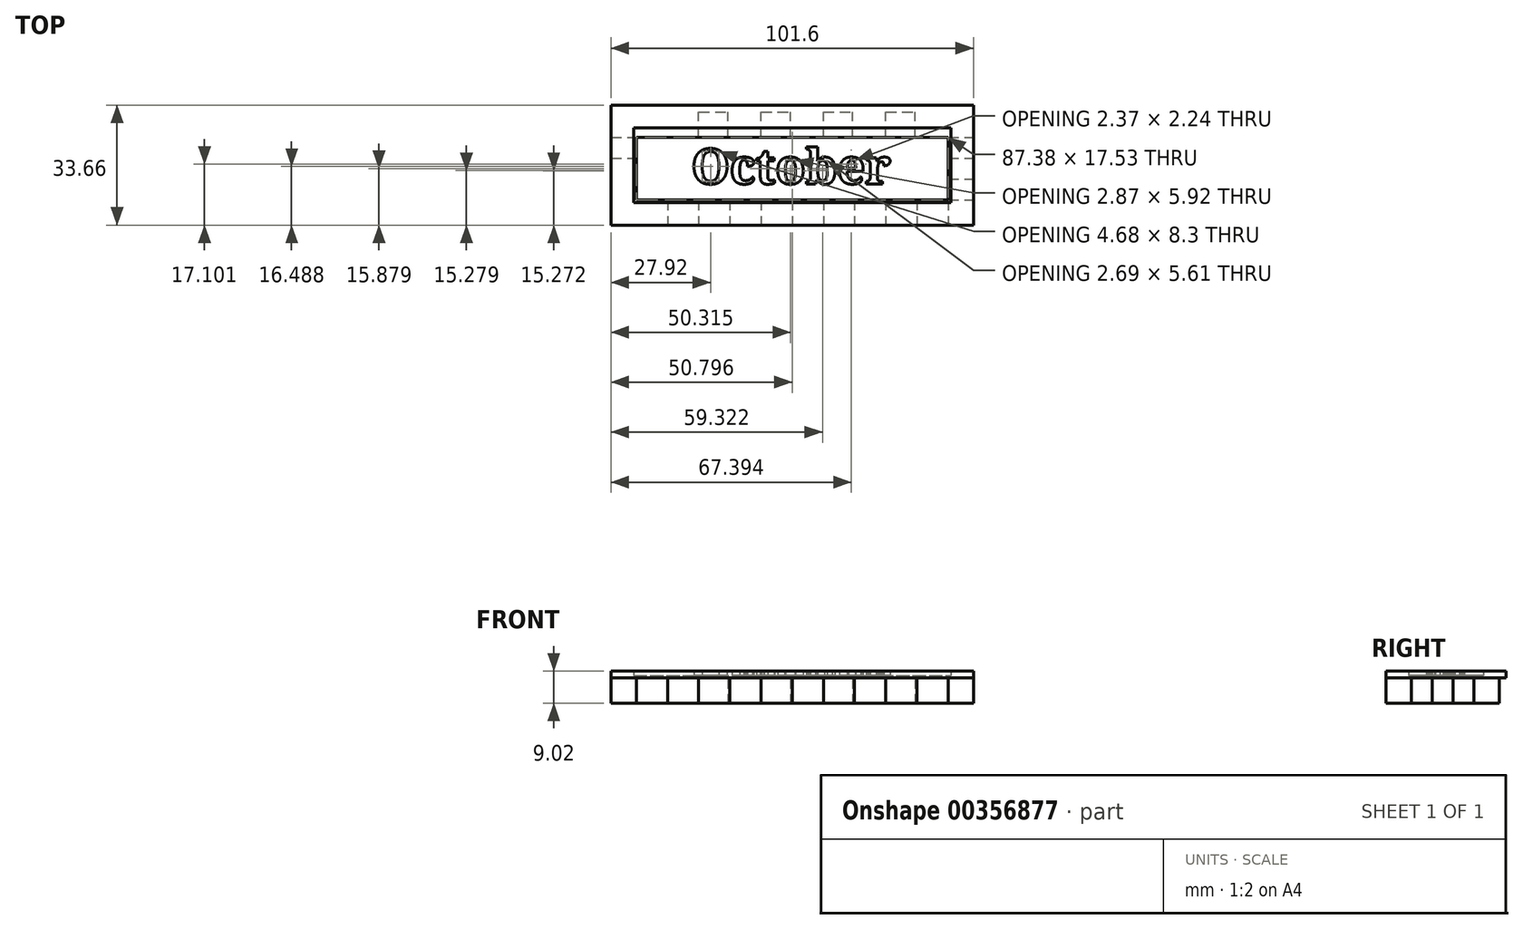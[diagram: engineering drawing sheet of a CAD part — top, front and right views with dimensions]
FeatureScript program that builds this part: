
annotation { "Feature Type Name" : "Feature", "Feature Type Description" : "" }
export const myFeature = defineFeature(function(context is Context, id is Id, definition is map)
    precondition{}
    {
        {
            var Q0;
            Q0=qCreatedBy(makeId("Top.planeOp"),FACE);
            var sketch = newSketch(context, id + "F0", { "sketchPlane" : qUnion([Q0])});
            skLineSegment(sketch, "E0.bottom", {"start": v(-52.12, 11.37) * mm, "end": v(49.48, 11.37) * mm});
            skLineSegment(sketch, "E0.top", {"start": v(-52.12, -20.38) * mm, "end": v(49.48, -20.38) * mm});
            skLineSegment(sketch, "E0.left", {"start": v(-52.12, 11.37) * mm, "end": v(-52.12, -20.38) * mm});
            skLineSegment(sketch, "E0.right", {"start": v(49.48, 11.37) * mm, "end": v(49.48, -20.38) * mm});
            skLineSegment(sketch, "E1.bottom", {"start": v(-52.12, 11.37) * mm, "end": v(-45.01, 11.37) * mm});
            skLineSegment(sketch, "E1.top", {"start": v(-52.12, 4.26) * mm, "end": v(-45.01, 4.26) * mm});
            skLineSegment(sketch, "E1.left", {"start": v(-52.12, 11.37) * mm, "end": v(-52.12, 4.26) * mm});
            skLineSegment(sketch, "E1.right", {"start": v(-45.01, 11.37) * mm, "end": v(-45.01, 4.26) * mm});
            skLineSegment(sketch, "E2.bottom", {"start": v(-45.01, 11.37) * mm, "end": v(-36.78, 11.37) * mm});
            skLineSegment(sketch, "E2.top", {"start": v(-45.01, 4.26) * mm, "end": v(-36.78, 4.26) * mm});
            skLineSegment(sketch, "E2.right", {"start": v(-36.78, 11.37) * mm, "end": v(-36.78, 4.26) * mm});
            skLineSegment(sketch, "E3.bottom", {"start": v(-36.78, 4.26) * mm, "end": v(-27.54, 4.26) * mm});
            skLineSegment(sketch, "E3.top", {"start": v(-36.78, 11.37) * mm, "end": v(-27.54, 11.37) * mm});
            skLineSegment(sketch, "E3.left", {"start": v(-36.78, 4.26) * mm, "end": v(-36.78, 11.37) * mm});
            skLineSegment(sketch, "E3.right", {"start": v(-27.54, 4.26) * mm, "end": v(-27.54, 11.37) * mm});
            skLineSegment(sketch, "E4.bottom", {"start": v(-27.54, 4.26) * mm, "end": v(-19.3, 4.26) * mm});
            skLineSegment(sketch, "E4.top", {"start": v(-27.54, 11.37) * mm, "end": v(-19.3, 11.37) * mm});
            skLineSegment(sketch, "E4.right", {"start": v(-19.3, 4.26) * mm, "end": v(-19.3, 11.37) * mm});
            skLineSegment(sketch, "E5.bottom", {"start": v(-19.3, 4.26) * mm, "end": v(-10.06, 4.26) * mm});
            skLineSegment(sketch, "E5.top", {"start": v(-19.3, 11.37) * mm, "end": v(-10.06, 11.37) * mm});
            skLineSegment(sketch, "E5.right", {"start": v(-10.06, 4.26) * mm, "end": v(-10.06, 11.37) * mm});
            skLineSegment(sketch, "E6.bottom", {"start": v(-10.06, 4.26) * mm, "end": v(-10.06, 4.26) * mm});
            skLineSegment(sketch, "E6.top", {"start": v(-10.06, 11.37) * mm, "end": v(-10.06, 11.37) * mm});
            skLineSegment(sketch, "E7.bottom", {"start": v(-10.06, 4.26) * mm, "end": v(-1.83, 4.26) * mm});
            skLineSegment(sketch, "E7.top", {"start": v(-10.06, 11.37) * mm, "end": v(-1.83, 11.37) * mm});
            skLineSegment(sketch, "E7.right", {"start": v(-1.83, 4.26) * mm, "end": v(-1.83, 11.37) * mm});
            skLineSegment(sketch, "E8.bottom", {"start": v(-1.83, 4.26) * mm, "end": v(7.41, 4.26) * mm});
            skLineSegment(sketch, "E8.top", {"start": v(-1.83, 11.37) * mm, "end": v(7.41, 11.37) * mm});
            skLineSegment(sketch, "E8.right", {"start": v(7.41, 4.26) * mm, "end": v(7.41, 11.37) * mm});
            skLineSegment(sketch, "E9.bottom", {"start": v(7.41, 4.26) * mm, "end": v(15.64, 4.26) * mm});
            skLineSegment(sketch, "E9.top", {"start": v(7.41, 11.37) * mm, "end": v(15.64, 11.37) * mm});
            skLineSegment(sketch, "E9.right", {"start": v(15.64, 4.26) * mm, "end": v(15.64, 11.37) * mm});
            skLineSegment(sketch, "E10.bottom", {"start": v(15.64, 4.26) * mm, "end": v(24.89, 4.26) * mm});
            skLineSegment(sketch, "E10.top", {"start": v(15.64, 11.37) * mm, "end": v(24.89, 11.37) * mm});
            skLineSegment(sketch, "E10.right", {"start": v(24.89, 4.26) * mm, "end": v(24.89, 11.37) * mm});
            skLineSegment(sketch, "E11.bottom", {"start": v(24.89, 4.26) * mm, "end": v(24.89, 4.26) * mm});
            skLineSegment(sketch, "E11.top", {"start": v(24.89, 11.37) * mm, "end": v(24.89, 11.37) * mm});
            skLineSegment(sketch, "E12.bottom", {"start": v(24.89, 4.26) * mm, "end": v(33.12, 4.26) * mm});
            skLineSegment(sketch, "E12.top", {"start": v(24.89, 11.37) * mm, "end": v(33.12, 11.37) * mm});
            skLineSegment(sketch, "E12.right", {"start": v(33.12, 4.26) * mm, "end": v(33.12, 11.37) * mm});
            skLineSegment(sketch, "E13.bottom", {"start": v(33.12, 4.26) * mm, "end": v(42.36, 4.26) * mm});
            skLineSegment(sketch, "E13.top", {"start": v(33.12, 11.37) * mm, "end": v(42.36, 11.37) * mm});
            skLineSegment(sketch, "E13.right", {"start": v(42.36, 4.26) * mm, "end": v(42.36, 11.37) * mm});
            skLineSegment(sketch, "E14.bottom", {"start": v(42.36, 4.26) * mm, "end": v(49.48, 4.26) * mm});
            skLineSegment(sketch, "E14.top", {"start": v(42.36, 11.37) * mm, "end": v(49.48, 11.37) * mm});
            skLineSegment(sketch, "E14.right", {"start": v(49.48, 4.26) * mm, "end": v(49.48, 11.37) * mm});
            skLineSegment(sketch, "E15.bottom", {"start": v(-52.12, -20.38) * mm, "end": v(-45.01, -20.38) * mm});
            skLineSegment(sketch, "E15.top", {"start": v(-52.12, -13.26) * mm, "end": v(-45.01, -13.26) * mm});
            skLineSegment(sketch, "E15.left", {"start": v(-52.12, -20.38) * mm, "end": v(-52.12, -13.26) * mm});
            skLineSegment(sketch, "E15.right", {"start": v(-45.01, -20.38) * mm, "end": v(-45.01, -13.26) * mm});
            skLineSegment(sketch, "E16.bottom", {"start": v(-45.01, -13.26) * mm, "end": v(-45.01, -13.26) * mm});
            skLineSegment(sketch, "E16.top", {"start": v(-45.01, -20.38) * mm, "end": v(-45.01, -20.38) * mm});
            skLineSegment(sketch, "E16.left", {"start": v(-45.01, -13.26) * mm, "end": v(-45.01, -20.38) * mm});
            skLineSegment(sketch, "E16.right", {"start": v(-45.01, -13.26) * mm, "end": v(-45.01, -20.38) * mm});
            skLineSegment(sketch, "E17.bottom", {"start": v(-45.01, -13.26) * mm, "end": v(-36.27, -13.26) * mm});
            skLineSegment(sketch, "E17.top", {"start": v(-45.01, -20.38) * mm, "end": v(-36.27, -20.38) * mm});
            skLineSegment(sketch, "E17.right", {"start": v(-36.27, -13.26) * mm, "end": v(-36.27, -20.38) * mm});
            skLineSegment(sketch, "E18.bottom", {"start": v(-36.27, -13.26) * mm, "end": v(-36.27, -13.26) * mm});
            skLineSegment(sketch, "E18.top", {"start": v(-36.27, -20.38) * mm, "end": v(-36.27, -20.38) * mm});
            skLineSegment(sketch, "E19.bottom", {"start": v(-36.27, -13.26) * mm, "end": v(-27.54, -13.26) * mm});
            skLineSegment(sketch, "E19.top", {"start": v(-36.27, -20.38) * mm, "end": v(-27.54, -20.38) * mm});
            skLineSegment(sketch, "E19.right", {"start": v(-27.54, -13.26) * mm, "end": v(-27.54, -20.38) * mm});
            skLineSegment(sketch, "E20.bottom", {"start": v(-27.54, -13.26) * mm, "end": v(-18.8, -13.26) * mm});
            skLineSegment(sketch, "E20.top", {"start": v(-27.54, -20.38) * mm, "end": v(-18.8, -20.38) * mm});
            skLineSegment(sketch, "E20.right", {"start": v(-18.8, -13.26) * mm, "end": v(-18.8, -20.38) * mm});
            skLineSegment(sketch, "E21.bottom", {"start": v(-18.8, -13.26) * mm, "end": v(-10.06, -13.26) * mm});
            skLineSegment(sketch, "E21.top", {"start": v(-18.8, -20.38) * mm, "end": v(-10.06, -20.38) * mm});
            skLineSegment(sketch, "E21.right", {"start": v(-10.06, -13.26) * mm, "end": v(-10.06, -20.38) * mm});
            skLineSegment(sketch, "E22.bottom", {"start": v(-10.06, -13.26) * mm, "end": v(-1.32, -13.26) * mm});
            skLineSegment(sketch, "E22.top", {"start": v(-10.06, -20.38) * mm, "end": v(-1.32, -20.38) * mm});
            skLineSegment(sketch, "E22.right", {"start": v(-1.32, -13.26) * mm, "end": v(-1.32, -20.38) * mm});
            skLineSegment(sketch, "E23.bottom", {"start": v(-1.32, -13.26) * mm, "end": v(7.41, -13.26) * mm});
            skLineSegment(sketch, "E23.top", {"start": v(-1.32, -20.38) * mm, "end": v(7.41, -20.38) * mm});
            skLineSegment(sketch, "E23.right", {"start": v(7.41, -13.26) * mm, "end": v(7.41, -20.38) * mm});
            skLineSegment(sketch, "E24.bottom", {"start": v(7.41, -13.26) * mm, "end": v(16.15, -13.26) * mm});
            skLineSegment(sketch, "E24.top", {"start": v(7.41, -20.38) * mm, "end": v(16.15, -20.38) * mm});
            skLineSegment(sketch, "E24.right", {"start": v(16.15, -13.26) * mm, "end": v(16.15, -20.38) * mm});
            skLineSegment(sketch, "E25.bottom", {"start": v(16.15, -13.26) * mm, "end": v(24.89, -13.26) * mm});
            skLineSegment(sketch, "E25.top", {"start": v(16.15, -20.38) * mm, "end": v(24.89, -20.38) * mm});
            skLineSegment(sketch, "E25.right", {"start": v(24.89, -13.26) * mm, "end": v(24.89, -20.38) * mm});
            skLineSegment(sketch, "E26.bottom", {"start": v(24.89, -13.26) * mm, "end": v(33.63, -13.26) * mm});
            skLineSegment(sketch, "E26.top", {"start": v(24.89, -20.38) * mm, "end": v(33.63, -20.38) * mm});
            skLineSegment(sketch, "E26.right", {"start": v(33.63, -13.26) * mm, "end": v(33.63, -20.38) * mm});
            skLineSegment(sketch, "E27.bottom", {"start": v(33.63, -13.26) * mm, "end": v(42.36, -13.26) * mm});
            skLineSegment(sketch, "E27.top", {"start": v(33.63, -20.38) * mm, "end": v(42.36, -20.38) * mm});
            skLineSegment(sketch, "E27.right", {"start": v(42.36, -13.26) * mm, "end": v(42.36, -20.38) * mm});
            skLineSegment(sketch, "E28.bottom", {"start": v(42.36, -13.26) * mm, "end": v(49.48, -13.26) * mm});
            skLineSegment(sketch, "E28.top", {"start": v(42.36, -20.38) * mm, "end": v(49.48, -20.38) * mm});
            skLineSegment(sketch, "E28.right", {"start": v(49.48, -13.26) * mm, "end": v(49.48, -20.38) * mm});
            skLineSegment(sketch, "E29.top", {"start": v(-52.12, -1.58) * mm, "end": v(-45.01, -1.58) * mm});
            skLineSegment(sketch, "E29.left", {"start": v(-52.12, 4.26) * mm, "end": v(-52.12, -1.58) * mm});
            skLineSegment(sketch, "E29.right", {"start": v(-45.01, 4.26) * mm, "end": v(-45.01, -1.58) * mm});
            skLineSegment(sketch, "E30.top", {"start": v(-52.12, -7.42) * mm, "end": v(-45.01, -7.42) * mm});
            skLineSegment(sketch, "E30.left", {"start": v(-52.12, -1.58) * mm, "end": v(-52.12, -7.42) * mm});
            skLineSegment(sketch, "E30.right", {"start": v(-45.01, -1.58) * mm, "end": v(-45.01, -7.42) * mm});
            skLineSegment(sketch, "E31.bottom", {"start": v(-45.01, -7.42) * mm, "end": v(-52.12, -7.42) * mm});
            skLineSegment(sketch, "E31.top", {"start": v(-45.01, -13.26) * mm, "end": v(-52.12, -13.26) * mm});
            skLineSegment(sketch, "E31.left", {"start": v(-45.01, -7.42) * mm, "end": v(-45.01, -13.26) * mm});
            skLineSegment(sketch, "E31.right", {"start": v(-52.12, -7.42) * mm, "end": v(-52.12, -13.26) * mm});
            skLineSegment(sketch, "E32.top", {"start": v(42.36, -1.58) * mm, "end": v(49.48, -1.58) * mm});
            skLineSegment(sketch, "E32.left", {"start": v(42.36, 4.26) * mm, "end": v(42.36, -1.58) * mm});
            skLineSegment(sketch, "E32.right", {"start": v(49.48, 4.26) * mm, "end": v(49.48, -1.58) * mm});
            skLineSegment(sketch, "E33.top", {"start": v(42.36, -7.42) * mm, "end": v(49.48, -7.42) * mm});
            skLineSegment(sketch, "E33.left", {"start": v(42.36, -1.58) * mm, "end": v(42.36, -7.42) * mm});
            skLineSegment(sketch, "E33.right", {"start": v(49.48, -1.58) * mm, "end": v(49.48, -7.42) * mm});
            skLineSegment(sketch, "E34.left", {"start": v(42.36, -7.42) * mm, "end": v(42.36, -13.26) * mm});
            skLineSegment(sketch, "E34.right", {"start": v(49.48, -7.42) * mm, "end": v(49.48, -13.26) * mm});
            skSolve(sketch);
        }
        {
            var Q0;
            Q0=makeQuery(id+"F0.imprint","IMPRINT",FACE,{"disambiguationData":[TD([[makeQuery(id+"F0.imprint","IMPRINT",EDGE,{"derivedFrom":sQuery(id+"F0.wireOp",EDGE,"E2.top")}),-1.0]])]});
            var Q1;
            Q1=makeQuery(id+"F0.imprint","IMPRINT",FACE,{"disambiguationData":[TD([[makeQuery(id+"F0.imprint","IMPRINT",EDGE,{"derivedFrom":sQuery(id+"F0.wireOp",EDGE,"E2.bottom")}),-1.0]])]});
            var Q2;
            Q2=makeQuery(id+"F0.imprint","IMPRINT",FACE,{"disambiguationData":[TD([[makeQuery(id+"F0.imprint","IMPRINT",EDGE,{"derivedFrom":sQuery(id+"F0.wireOp",EDGE,"E4.bottom")}),1.0]])]});
            var Q3;
            Q3=makeQuery(id+"F0.imprint","IMPRINT",FACE,{"disambiguationData":[TD([[makeQuery(id+"F0.imprint","IMPRINT",EDGE,{"derivedFrom":sQuery(id+"F0.wireOp",EDGE,"E7.bottom")}),1.0]])]});
            var Q4;
            Q4=makeQuery(id+"F0.imprint","IMPRINT",FACE,{"disambiguationData":[TD([[makeQuery(id+"F0.imprint","IMPRINT",EDGE,{"derivedFrom":sQuery(id+"F0.wireOp",EDGE,"E9.bottom")}),1.0]])]});
            var Q5;
            Q5=makeQuery(id+"F0.imprint","IMPRINT",FACE,{"disambiguationData":[TD([[makeQuery(id+"F0.imprint","IMPRINT",EDGE,{"derivedFrom":sQuery(id+"F0.wireOp",EDGE,"E12.bottom")}),1.0]])]});
            var Q6;
            Q6=makeQuery(id+"F0.imprint","IMPRINT",FACE,{"disambiguationData":[TD([[makeQuery(id+"F0.imprint","IMPRINT",EDGE,{"derivedFrom":sQuery(id+"F0.wireOp",EDGE,"E14.bottom")}),-1.0]])]});
            var Q7;
            Q7=makeQuery(id+"F0.imprint","IMPRINT",FACE,{"disambiguationData":[TD([[makeQuery(id+"F0.imprint","IMPRINT",EDGE,{"derivedFrom":sQuery(id+"F0.wireOp",EDGE,"E33.top")}),-1.0]])]});
            var Q8;
            Q8=makeQuery(id+"F0.imprint","IMPRINT",FACE,{"disambiguationData":[TD([[makeQuery(id+"F0.imprint","IMPRINT",EDGE,{"derivedFrom":sQuery(id+"F0.wireOp",EDGE,"E27.bottom")}),-1.0]])]});
            var Q9;
            Q9=makeQuery(id+"F0.imprint","IMPRINT",FACE,{"disambiguationData":[TD([[makeQuery(id+"F0.imprint","IMPRINT",EDGE,{"derivedFrom":sQuery(id+"F0.wireOp",EDGE,"E25.bottom")}),-1.0]])]});
            var Q10;
            Q10=makeQuery(id+"F0.imprint","IMPRINT",FACE,{"disambiguationData":[TD([[makeQuery(id+"F0.imprint","IMPRINT",EDGE,{"derivedFrom":sQuery(id+"F0.wireOp",EDGE,"E23.bottom")}),-1.0]])]});
            var Q11;
            Q11=makeQuery(id+"F0.imprint","IMPRINT",FACE,{"disambiguationData":[TD([[makeQuery(id+"F0.imprint","IMPRINT",EDGE,{"derivedFrom":sQuery(id+"F0.wireOp",EDGE,"E21.bottom")}),-1.0]])]});
            var Q12;
            Q12=makeQuery(id+"F0.imprint","IMPRINT",FACE,{"disambiguationData":[TD([[makeQuery(id+"F0.imprint","IMPRINT",EDGE,{"derivedFrom":sQuery(id+"F0.wireOp",EDGE,"E19.bottom")}),-1.0]])]});
            var Q13;
            Q13=makeQuery(id+"F0.imprint","IMPRINT",FACE,{"disambiguationData":[TD([[makeQuery(id+"F0.imprint","IMPRINT",EDGE,{"derivedFrom":sQuery(id+"F0.wireOp",EDGE,"E31.bottom")}),1.0]])]});
            var Q14;
            Q14=makeQuery(id+"F0.imprint","IMPRINT",FACE,{"disambiguationData":[TD([[makeQuery(id+"F0.imprint","IMPRINT",EDGE,{"derivedFrom":sQuery(id+"F0.wireOp",EDGE,"E1.top")}),-1.0]])]});
            extrude(context, id + "F1", {"entities" : qUnion([Q0, Q1, Q2, Q3, Q4, Q5, Q6, Q7, Q8, Q9, Q10, Q11, Q12, Q13, Q14]), "depth" : 7.11 * mm});
        }
        {
            var Q0;
            Q0=makeQuery(id+"F1.opExtrude","CAP_FACE",FACE,{"disambiguationData":[OSD([sQuery(id+"F0.wireOp",EDGE,"E2.bottom"),sQuery(id+"F0.wireOp",EDGE,"E1.right"),sQuery(id+"F0.wireOp",EDGE,"E3.bottom"),sQuery(id+"F0.wireOp",EDGE,"E3.left"),sQuery(id+"F0.wireOp",EDGE,"E4.top"),sQuery(id+"F0.wireOp",EDGE,"E3.right"),sQuery(id+"F0.wireOp",EDGE,"E5.bottom"),sQuery(id+"F0.wireOp",EDGE,"E4.right"),sQuery(id+"F0.wireOp",EDGE,"E6.top"),sQuery(id+"F0.wireOp",EDGE,"E5.right"),sQuery(id+"F0.wireOp",EDGE,"E7.bottom"),sQuery(id+"F0.wireOp",EDGE,"E5.right"),sQuery(id+"F0.wireOp",EDGE,"E8.top"),sQuery(id+"F0.wireOp",EDGE,"E7.right"),sQuery(id+"F0.wireOp",EDGE,"E9.bottom"),sQuery(id+"F0.wireOp",EDGE,"E8.right"),sQuery(id+"F0.wireOp",EDGE,"E10.top"),sQuery(id+"F0.wireOp",EDGE,"E9.right"),sQuery(id+"F0.wireOp",EDGE,"E11.bottom"),sQuery(id+"F0.wireOp",EDGE,"E10.right"),sQuery(id+"F0.wireOp",EDGE,"E12.top"),sQuery(id+"F0.wireOp",EDGE,"E10.right"),sQuery(id+"F0.wireOp",EDGE,"E13.bottom"),sQuery(id+"F0.wireOp",EDGE,"E12.right"),sQuery(id+"F0.wireOp",EDGE,"E16.bottom"),sQuery(id+"F0.wireOp",EDGE,"E17.top"),sQuery(id+"F0.wireOp",EDGE,"E16.left"),sQuery(id+"F0.wireOp",EDGE,"E18.bottom"),sQuery(id+"F0.wireOp",EDGE,"E17.right"),sQuery(id+"F0.wireOp",EDGE,"E19.top"),sQuery(id+"F0.wireOp",EDGE,"E17.right"),sQuery(id+"F0.wireOp",EDGE,"E20.bottom"),sQuery(id+"F0.wireOp",EDGE,"E19.right"),sQuery(id+"F0.wireOp",EDGE,"E21.top"),sQuery(id+"F0.wireOp",EDGE,"E20.right"),sQuery(id+"F0.wireOp",EDGE,"E22.bottom"),sQuery(id+"F0.wireOp",EDGE,"E21.right"),sQuery(id+"F0.wireOp",EDGE,"E23.top"),sQuery(id+"F0.wireOp",EDGE,"E22.right"),sQuery(id+"F0.wireOp",EDGE,"E24.bottom"),sQuery(id+"F0.wireOp",EDGE,"E23.right"),sQuery(id+"F0.wireOp",EDGE,"E25.top"),sQuery(id+"F0.wireOp",EDGE,"E24.right"),sQuery(id+"F0.wireOp",EDGE,"E26.bottom"),sQuery(id+"F0.wireOp",EDGE,"E25.right"),sQuery(id+"F0.wireOp",EDGE,"E27.top"),sQuery(id+"F0.wireOp",EDGE,"E26.right"),sQuery(id+"F0.wireOp",EDGE,"E27.right"),sQuery(id+"F0.wireOp",EDGE,"E1.top"),sQuery(id+"F0.wireOp",EDGE,"E29.left"),sQuery(id+"F0.wireOp",EDGE,"E29.top"),sQuery(id+"F0.wireOp",EDGE,"E30.right"),sQuery(id+"F0.wireOp",EDGE,"E31.bottom"),sQuery(id+"F0.wireOp",EDGE,"E31.top"),sQuery(id+"F0.wireOp",EDGE,"E31.right"),sQuery(id+"F0.wireOp",EDGE,"E14.bottom"),sQuery(id+"F0.wireOp",EDGE,"E32.right"),sQuery(id+"F0.wireOp",EDGE,"E32.top"),sQuery(id+"F0.wireOp",EDGE,"E33.left"),sQuery(id+"F0.wireOp",EDGE,"E33.top"),sQuery(id+"F0.wireOp",EDGE,"E28.bottom"),sQuery(id+"F0.wireOp",EDGE,"E34.right")])],"isStart":false});
            var sketch = newSketch(context, id + "F2", { "sketchPlane" : qUnion([Q0])});
            skLineSegment(sketch, "E35.bottom", {"start": v(-52.12, -20.38) * mm, "end": v(-45.01, -20.38) * mm});
            skLineSegment(sketch, "E35.top", {"start": v(-52.12, 13.28) * mm, "end": v(-45.01, 13.28) * mm});
            skLineSegment(sketch, "E35.left", {"start": v(-52.12, -20.38) * mm, "end": v(-52.12, 13.28) * mm});
            skLineSegment(sketch, "E35.right", {"start": v(-45.01, -20.38) * mm, "end": v(-45.01, 13.28) * mm});
            skLineSegment(sketch, "E36.bottom", {"start": v(-52.12, -20.38) * mm, "end": v(49.48, -20.38) * mm});
            skLineSegment(sketch, "E36.top", {"start": v(-52.12, -13.26) * mm, "end": v(49.48, -13.26) * mm});
            skLineSegment(sketch, "E36.left", {"start": v(-52.12, -20.38) * mm, "end": v(-52.12, -13.26) * mm});
            skLineSegment(sketch, "E36.right", {"start": v(49.48, -20.38) * mm, "end": v(49.48, -13.26) * mm});
            skPoint(sketch, "E37.oppositeSnap0", {"position": v(42.36, -4.5) * mm});
            skLineSegment(sketch, "E37.bottom", {"start": v(49.48, -20.38) * mm, "end": v(42.36, -20.38) * mm});
            skLineSegment(sketch, "E37.top", {"start": v(49.48, 13.28) * mm, "end": v(42.36, 13.28) * mm});
            skLineSegment(sketch, "E37.left", {"start": v(49.48, -20.38) * mm, "end": v(49.48, 13.28) * mm});
            skLineSegment(sketch, "E37.right", {"start": v(42.36, -20.38) * mm, "end": v(42.36, 13.28) * mm});
            skLineSegment(sketch, "E38.bottom", {"start": v(-52.12, 13.28) * mm, "end": v(49.48, 13.28) * mm});
            skLineSegment(sketch, "E38.top", {"start": v(-52.12, 4.26) * mm, "end": v(49.48, 4.26) * mm});
            skLineSegment(sketch, "E38.left", {"start": v(-52.12, 13.28) * mm, "end": v(-52.12, 4.26) * mm});
            skLineSegment(sketch, "E38.right", {"start": v(49.48, 13.28) * mm, "end": v(49.48, 4.26) * mm});
            skSolve(sketch);
        }
        {
            var Q0;
            Q0=qSketchRegion(id+"F2",true);
            var Q1;
            {var subQ5=sQuery(id+"F2.wireOp",EDGE,"E36.top");var subQ10=sQuery(id+"F2.wireOp",EDGE,"E35.right");var subQ12=makeQuery(id+"F2.imprint","INTERSECT",VERTEX,{"derivedFrom":[makeQuery(id+"F1.opExtrude","CAP_EDGE",EDGE,{"disambiguationData":[OSD([sQuery(id+"F0.wireOp",EDGE,"E31.bottom")])],"isStart":false}),subQ10]});var subQ24=makeQuery(id+"F2.imprint","INTERSECT",VERTEX,{"derivedFrom":[subQ10,subQ5]});Q1=makeQuery(id+"F2.imprint","IMPRINT",FACE,{"disambiguationData":[TD([[makeQuery(id+"F2.imprint","IMPRINT",EDGE,{"disambiguationData":[TD([[subQ12,1.0],[subQ24,-1.0]])],"derivedFrom":subQ10}),-1.0]])]});}
            extrude(context, id + "F3", {"entities" : qUnion([Q0, Q1]), "depth" : 0.64 * mm});
        }
        {
            var Q0;
            Q0=makeQuery(id+"F3.opExtrude","CAP_FACE",FACE,{"disambiguationData":[OSD([sQuery(id+"F2.wireOp",EDGE,"E35.left"),sQuery(id+"F2.wireOp",EDGE,"E36.bottom"),sQuery(id+"F2.wireOp",EDGE,"E36.left"),sQuery(id+"F2.wireOp",EDGE,"E37.bottom"),sQuery(id+"F2.wireOp",EDGE,"E37.left"),sQuery(id+"F2.wireOp",EDGE,"E38.bottom"),sQuery(id+"F2.wireOp",EDGE,"E38.left"),sQuery(id+"F2.wireOp",EDGE,"E38.right")])],"isStart":false});
            var sketch = newSketch(context, id + "F4", { "sketchPlane" : qUnion([Q0])});
            skLineSegment(sketch, "E39.bottom", {"start": v(-52.12, 13.28) * mm, "end": v(49.48, 13.28) * mm});
            skLineSegment(sketch, "E39.top", {"start": v(-52.12, 6.93) * mm, "end": v(49.48, 6.93) * mm});
            skLineSegment(sketch, "E39.left", {"start": v(-52.12, 13.28) * mm, "end": v(-52.12, 6.93) * mm});
            skLineSegment(sketch, "E39.right", {"start": v(49.48, 13.28) * mm, "end": v(49.48, 6.93) * mm});
            skLineSegment(sketch, "E40.bottom", {"start": v(-52.12, 13.28) * mm, "end": v(-45.77, 13.28) * mm});
            skLineSegment(sketch, "E40.top", {"start": v(-52.12, -20.38) * mm, "end": v(-45.77, -20.38) * mm});
            skLineSegment(sketch, "E40.left", {"start": v(-52.12, 13.28) * mm, "end": v(-52.12, -20.38) * mm});
            skLineSegment(sketch, "E40.right", {"start": v(-45.77, 13.28) * mm, "end": v(-45.77, -20.38) * mm});
            skLineSegment(sketch, "E41.bottom", {"start": v(-52.12, -14.03) * mm, "end": v(49.48, -14.03) * mm});
            skLineSegment(sketch, "E41.top", {"start": v(-52.12, -20.38) * mm, "end": v(49.48, -20.38) * mm});
            skLineSegment(sketch, "E41.left", {"start": v(-52.12, -14.03) * mm, "end": v(-52.12, -20.38) * mm});
            skLineSegment(sketch, "E41.right", {"start": v(49.48, -14.03) * mm, "end": v(49.48, -20.38) * mm});
            skLineSegment(sketch, "E42.bottom", {"start": v(49.48, -20.38) * mm, "end": v(43.13, -20.38) * mm});
            skLineSegment(sketch, "E42.top", {"start": v(49.48, 13.28) * mm, "end": v(43.13, 13.28) * mm});
            skLineSegment(sketch, "E42.left", {"start": v(49.48, -20.38) * mm, "end": v(49.48, 13.28) * mm});
            skLineSegment(sketch, "E42.right", {"start": v(43.13, -20.38) * mm, "end": v(43.13, 13.28) * mm});
            skSolve(sketch);
        }
        {
            var Q0;
            Q0=qSketchRegion(id+"F4",true);
            extrude(context, id + "F5", {"entities" : qUnion([Q0]), "operationType" : NewBodyOperationType.ADD, "depth" : 1.27 * mm});
        }
        {
            var Q0;
            Q0=makeQuery(id+"F3.opExtrude","CAP_FACE",FACE,{"disambiguationData":[OSD([sQuery(id+"F2.wireOp",EDGE,"E35.left"),sQuery(id+"F2.wireOp",EDGE,"E36.bottom"),sQuery(id+"F2.wireOp",EDGE,"E36.left"),sQuery(id+"F2.wireOp",EDGE,"E37.bottom"),sQuery(id+"F2.wireOp",EDGE,"E37.left"),sQuery(id+"F2.wireOp",EDGE,"E38.bottom"),sQuery(id+"F2.wireOp",EDGE,"E38.left"),sQuery(id+"F2.wireOp",EDGE,"E38.right")])],"isStart":false});
            var sketch = newSketch(context, id + "F6", { "sketchPlane" : qUnion([Q0])});
            skText(sketch, "E43", { "text": "October", "fontName": "NotoSerif-Bold.ttf"});
            const initialGuessF6  = {"E43": [-0.0296, -0.0088, 1, 0, 0.00988]};
            skSetInitialGuess(sketch, initialGuessF6);
            skSolve(sketch);
        }
        {
            var Q0;
            Q0 = qSketchRegion(id + "F6", true);
            extrude(context, id + "F7", {"entities" : qUnion([Q0]), "operationType" : NewBodyOperationType.ADD, "depth" : 1.27 * mm});
        }
    });
